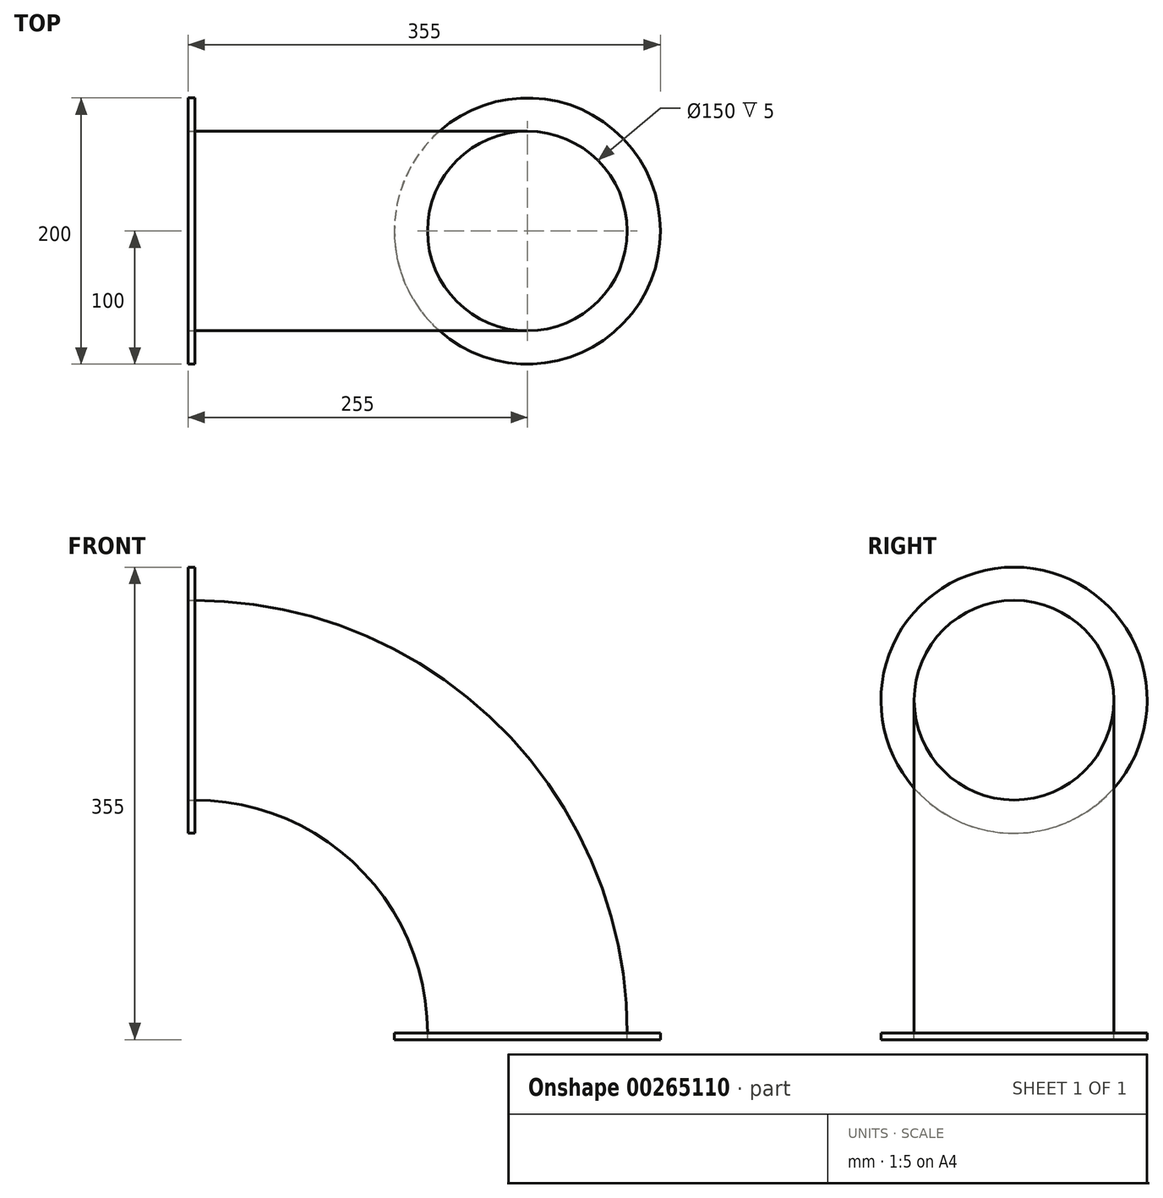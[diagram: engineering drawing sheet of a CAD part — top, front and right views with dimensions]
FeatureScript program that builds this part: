
annotation { "Feature Type Name" : "Feature", "Feature Type Description" : "" }
export const myFeature = defineFeature(function(context is Context, id is Id, definition is map)
    precondition{}
    {
        {
            var Q0;
            Q0=qCreatedBy(makeId("Front.planeOp"),FACE);
            var sketch = newSketch(context, id + "F0", { "sketchPlane" : qUnion([Q0])});
            skArc(sketch, "E0", {"start": v(250, 0) * mm, "mid": v(176.78, 176.78) * mm, "end": v(0, 250) * mm, "construction": true});
            skArc(sketch, "E1", {"start": v(250, 0) * mm, "mid": v(176.78, 176.78) * mm, "end": v(0, 250) * mm});
            skSolve(sketch);
        }
        {
            var Q0;
            Q0=qCreatedBy(makeId("Top.planeOp"),FACE);
            var sketch = newSketch(context, id + "F1", { "sketchPlane" : qUnion([Q0])});
            skCircle(sketch, "E2", {"center": v(250, 0) * mm, "radius": 75 * mm});
            skSolve(sketch);
        }
        {
            var Q0;
            Q0=makeQuery(id+"F1.imprint","IMPRINT",FACE,{"disambiguationData":[TD([[makeQuery(id+"F1.imprint","IMPRINT",EDGE,{"derivedFrom":sQuery(id+"F1.wireOp",EDGE,"E2")}),1.0]])]});
            var Q1;
            Q1=sQuery(id+"F0.wireOp",EDGE,"E1");
            sweep(context, id + "F2", {"profiles" : qUnion([Q0]), "path" : qUnion([Q1])});
        }
        {
            var Q0;
            Q0=makeQuery(id+"F2.opSweep","CAP_FACE",FACE,{"disambiguationData":[OSD([sQuery(id+"F0.wireOp",VERTEX,"E1.start"),sQuery(id+"F1.wireOp",EDGE,"E2")])],"isStart":true});
            var sketch = newSketch(context, id + "F3", { "sketchPlane" : qUnion([Q0])});
            skCircle(sketch, "E3", {"center": v(250, 0) * mm, "radius": 100 * mm});
            skSolve(sketch);
        }
        {
            var Q0;
            Q0=makeQuery(id+"F3.imprint","IMPRINT",FACE,{"disambiguationData":[TD([[makeQuery(id+"F3.imprint","IMPRINT",EDGE,{"derivedFrom":sQuery(id+"F3.wireOp",EDGE,"E3")}),1.0]])]});
            extrude(context, id + "F4", {"entities" : qUnion([Q0]), "depth" : 5 * mm});
        }
        {
            var Q0;
            Q0=makeQuery(id+"F2.opSweep","CAP_FACE",FACE,{"disambiguationData":[OSD([sQuery(id+"F0.wireOp",VERTEX,"E1.end"),sQuery(id+"F1.wireOp",EDGE,"E2")])],"isStart":false});
            var sketch = newSketch(context, id + "F5", { "sketchPlane" : qUnion([Q0])});
            skCircle(sketch, "E4", {"center": v(0, 250) * mm, "radius": 100 * mm});
            skSolve(sketch);
        }
        {
            var Q0;
            Q0=makeQuery(id+"F5.imprint","IMPRINT",FACE,{"disambiguationData":[TD([[makeQuery(id+"F5.imprint","IMPRINT",EDGE,{"derivedFrom":sQuery(id+"F5.wireOp",EDGE,"E4")}),1.0]])]});
            extrude(context, id + "F6", {"entities" : qUnion([Q0]), "depth" : 5 * mm});
        }
    });
